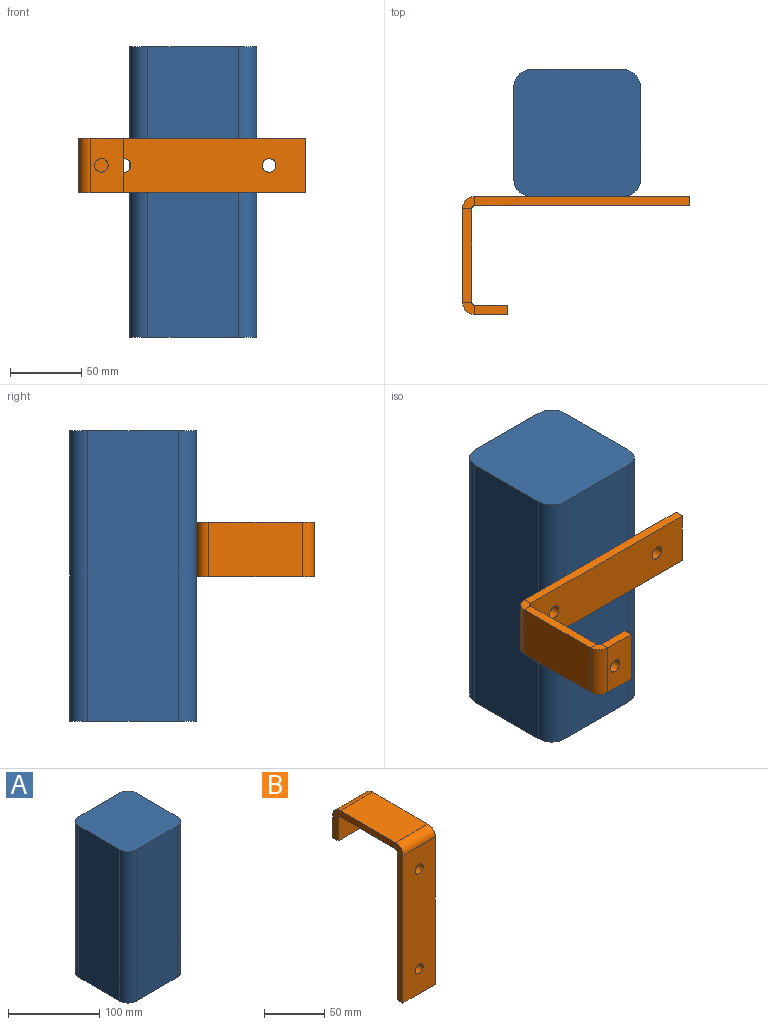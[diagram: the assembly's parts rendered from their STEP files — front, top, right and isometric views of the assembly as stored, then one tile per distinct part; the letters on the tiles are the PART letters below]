
ASSEMBLY  parts=2 mates=2
PART A: 10 faces, bbox 88.9x88.9x203.2 mm
  f0: plane 203.2x63.5mm, normal (-1,0,0), area 12903.2mm2, adj f4,f5,f6,f9
  f1: plane 203.2x63.5mm, normal (0,-1,0), area 12903.2mm2, adj f4,f5,f6,f7
  f2: plane 203.2x63.5mm, normal (1,0,0), area 12903.2mm2, adj f4,f5,f7,f8
  f3: plane 203.2x63.5mm, normal (0,1,0), area 12903.2mm2, adj f4,f5,f8,f9
  f4: plane 88.9x88.9mm, normal (0,0,1), area 7764.8mm2, adj f0,f1,f2,f3,f6,f7,f8,f9
  f5: plane 88.9x88.9mm, normal (0,0,-1), area 7764.8mm2, adj f0,f1,f2,f3,f6,f7,f8,f9
  f6: cylinder r=12.7mm len=203.2mm, axis (0,0,-1), area 4053.7mm2, adj f0,f1,f4,f5
  f7: cylinder r=12.7mm len=203.2mm, axis (0,0,1), area 4053.7mm2, adj f1,f2,f4,f5
  f8: cylinder r=12.7mm len=203.2mm, axis (0,0,-1), area 4053.7mm2, adj f2,f3,f4,f5
  f9: cylinder r=12.7mm len=203.2mm, axis (0,0,1), area 4053.7mm2, adj f0,f3,f4,f5
PART B: 25 faces, bbox 38.1x82.6x158.8 mm
  f0: plane 38.1x6.35mm, normal (0,0,-1), area 241.9mm2, adj f1,f4,f5,f6
  f1: plane 150.11x6.35mm, normal (1,0,0), area 953.2mm2, adj f0,f5,f6,f21
  f2: cylinder r=4.76mm len=9.53mm, axis (0,-1,0), area 190mm2, adj f5,f6
  f3: cylinder r=4.76mm len=9.53mm, axis (0,-1,0), area 190mm2, adj f5,f6
  f4: plane 150.11x6.35mm, normal (-1,0,0), area 953.2mm2, adj f0,f5,f6,f22
  f5: plane 150.11x38.1mm, normal (0,-1,0), area 5576.8mm2, adj f0,f1,f2,f3,f4,f23
  f6: plane 150.11x38.1mm, normal (0,1,0), area 5576.8mm2, adj f0,f1,f2,f3,f4,f24
  f7: plane 65.28x6.35mm, normal (-1,0,0), area 414.5mm2, adj f9,f10,f18,f22
  f8: plane 65.28x6.35mm, normal (1,0,0), area 414.5mm2, adj f9,f10,f17,f21
  f9: plane 65.28x38.1mm, normal (0,0,1), area 2487.1mm2, adj f7,f8,f19,f23
  f10: plane 65.28x38.1mm, normal (0,0,-1), area 2487.1mm2, adj f7,f8,f20,f24
  f11: plane 23.11x6.35mm, normal (-1,0,0), area 146.8mm2, adj f14,f15,f16,f18
  f12: plane 23.11x6.35mm, normal (1,0,0), area 146.8mm2, adj f14,f15,f16,f17
  f13: cylinder r=4.76mm len=9.53mm, axis (0,1,0), area 190mm2, adj f15,f16
  f14: plane 38.1x6.35mm, normal (0,0,-1), area 241.9mm2, adj f11,f12,f15,f16
  f15: plane 38.1x23.11mm, normal (0,1,0), area 809.4mm2, adj f11,f12,f13,f14,f19
  f16: plane 38.1x23.11mm, normal (0,-1,0), area 809.4mm2, adj f11,f12,f13,f14,f20
  f17: plane 8.64x8.64mm, normal (1,0,0), area 54.5mm2, adj f8,f12,f19,f20
  f18: plane 8.64x8.64mm, normal (-1,0,0), area 54.5mm2, adj f7,f11,f19,f20
  f19: cylinder r=8.64mm len=38.1mm, axis (1,0,0), area 516.8mm2, adj f9,f15,f17,f18
  f20: cylinder r=2.29mm len=38.1mm, axis (1,0,0), area 136.8mm2, adj f10,f16,f17,f18
  f21: plane 8.64x8.64mm, normal (1,0,0), area 54.5mm2, adj f1,f8,f23,f24
  f22: plane 8.64x8.64mm, normal (-1,0,0), area 54.5mm2, adj f4,f7,f23,f24
  f23: cylinder r=8.64mm len=38.1mm, axis (1,0,0), area 516.8mm2, adj f5,f9,f21,f22
  f24: cylinder r=2.29mm len=38.1mm, axis (1,0,0), area 136.8mm2, adj f6,f10,f21,f22
PLACE A t=(-2.92,8.96,-43.8)mm fixed
PLACE B rot(axis=(0.71,0,-0.71),180deg) t=(75.62,-38.66,76.42)mm
MATE planar B.f5 <-> A.f1  axis (0,1,0) through (0.6,-35.49,76.42)mm
MATE parallel B.f10 <-> A.f2  axis (1,0,0) through (-76.78,-76.76,76.42)mm
